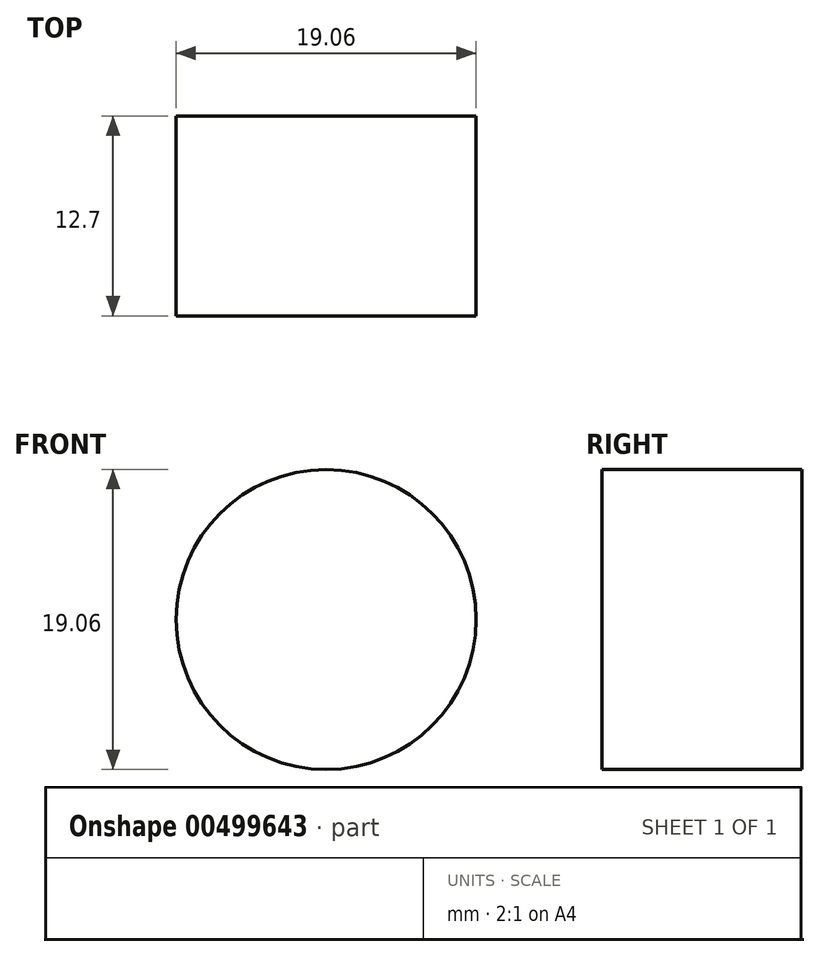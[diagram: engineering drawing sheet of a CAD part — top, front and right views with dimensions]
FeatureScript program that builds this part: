
annotation { "Feature Type Name" : "Feature", "Feature Type Description" : "" }
export const myFeature = defineFeature(function(context is Context, id is Id, definition is map)
    precondition{}
    {
        {
            var Q0;
            Q0=qCreatedBy(makeId("Front.planeOp"),FACE);
            var sketch = newSketch(context, id + "F0", { "sketchPlane" : qUnion([Q0])});
            skCircle(sketch, "E0", {"center": v(0, 0) * mm, "radius": 9.53 * mm});
            skSolve(sketch);
        }
        {
            var Q0;
            Q0 = qSketchRegion(id + "F0", true);
            extrude(context, id + "F1", {"entities" : qUnion([Q0]), "depth" : 6.35 * mm, "hasSecondDirection" : true, "secondDirectionOppositeDirection" : true, "secondDirectionDepth" : 6.35 * mm});
        }
    });
